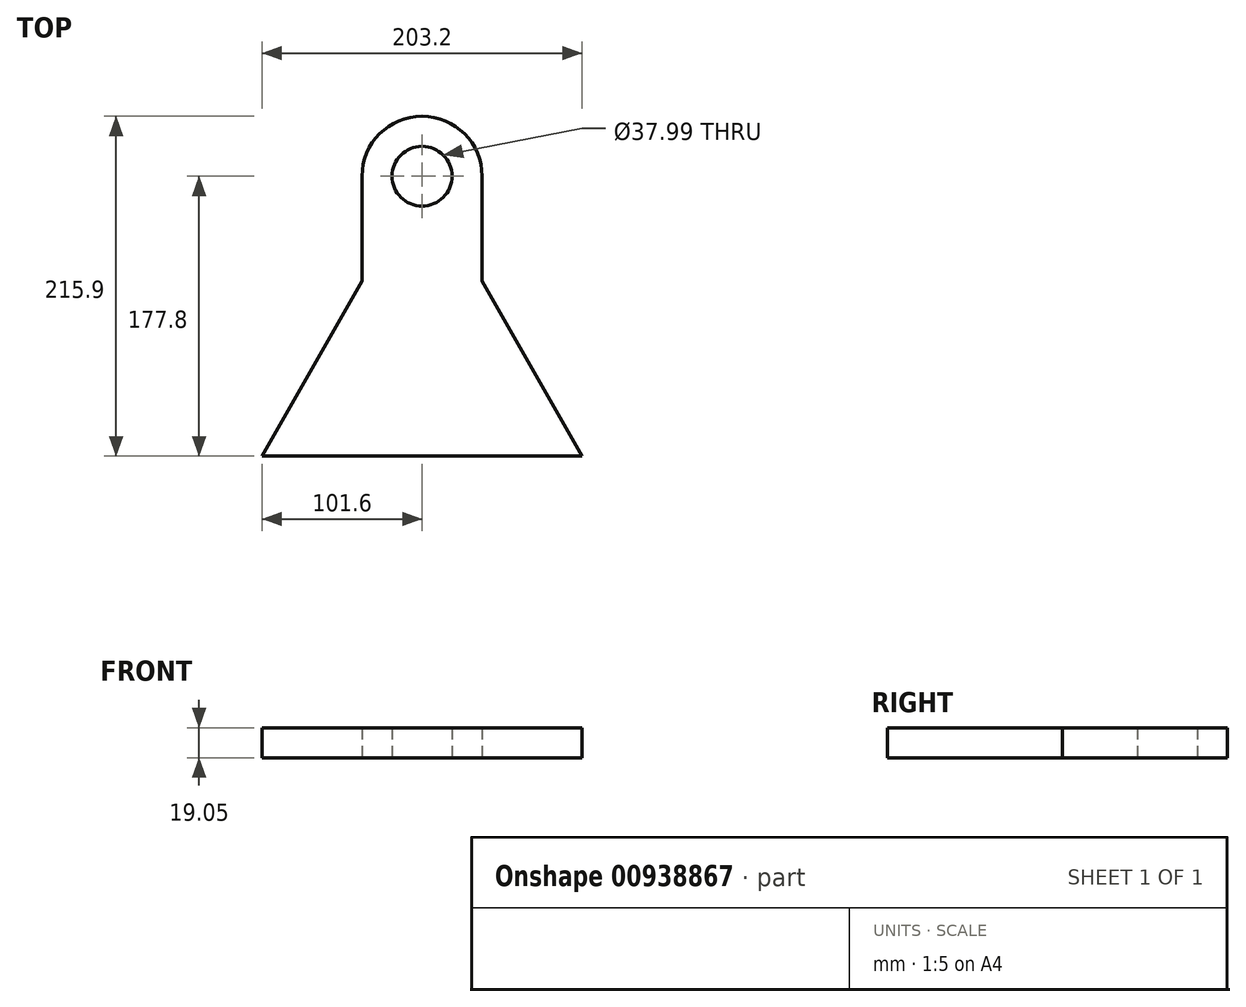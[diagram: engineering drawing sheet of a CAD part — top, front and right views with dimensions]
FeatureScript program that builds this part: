
annotation { "Feature Type Name" : "Feature", "Feature Type Description" : "" }
export const myFeature = defineFeature(function(context is Context, id is Id, definition is map)
    precondition{}
    {
        {
            var Q0;
            Q0=qCreatedBy(makeId("Top.planeOp"),FACE);
            var sketch = newSketch(context, id + "F0", { "sketchPlane" : qUnion([Q0])});
            skLineSegment(sketch, "E0", {"start": v(-101.6, 0) * mm, "end": v(101.6, 0) * mm});
            skLineSegment(sketch, "E1", {"start": v(0, 177.8) * mm, "end": v(0, 0) * mm, "construction": true});
            skLineSegment(sketch, "E2", {"start": v(-101.6, 0) * mm, "end": v(-38.1, 111.12) * mm});
            skLineSegment(sketch, "E3", {"start": v(38.1, 111.13) * mm, "end": v(101.6, 0) * mm});
            skLineSegment(sketch, "E4.bottom", {"start": v(0, 215.9) * mm, "end": v(0, 215.9) * mm});
            skLineSegment(sketch, "E4.left", {"start": v(38.1, 177.8) * mm, "end": v(38.1, 139.7) * mm});
            skLineSegment(sketch, "E4.right", {"start": v(-38.1, 177.8) * mm, "end": v(-38.1, 139.7) * mm});
            skPoint(sketch, "E4.middle", {"position": v(0, 177.8) * mm});
            skPoint(sketch, "E5.visualSharp", {"position": v(-38.1, 215.9) * mm});
            skArc(sketch, "E5.filletArc", {"start": v(0, 215.9) * mm, "mid": v(-26.94, 204.74) * mm, "end": v(-38.1, 177.8) * mm});
            skPoint(sketch, "E6.visualSharp", {"position": v(38.1, 215.9) * mm});
            skArc(sketch, "E6.filletArc", {"start": v(38.1, 177.8) * mm, "mid": v(26.94, 204.74) * mm, "end": v(0, 215.9) * mm});
            skLineSegment(sketch, "E7", {"start": v(-38.1, 139.7) * mm, "end": v(-38.1, 111.12) * mm});
            skLineSegment(sketch, "E8", {"start": v(38.1, 139.7) * mm, "end": v(38.1, 111.13) * mm});
            skCircle(sketch, "E9", {"center": v(0, 177.8) * mm, "radius": 19 * mm});
            skSolve(sketch);
        }
        {
            var Q0;
            Q0 = qSketchRegion(id + "F0", true);
            extrude(context, id + "F1", {"entities" : qUnion([Q0]), "depth" : 19.05 * mm, "offsetDistance" : 25.4 * mm});
        }
    });
